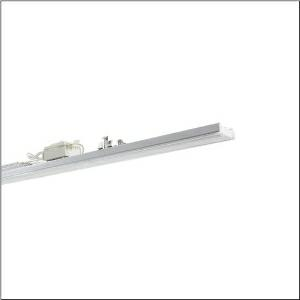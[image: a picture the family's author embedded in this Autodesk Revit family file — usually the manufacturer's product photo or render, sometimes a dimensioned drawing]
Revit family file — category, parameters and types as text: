
# Revit family: licross_r__21_recessed_mo_52te14dn49xg_1976
name_source: partatom
category: Lighting Fixtures
units: mm (PartAtom-declared; Revit-internal decimal feet)

## family parameters
Cut with Voids When Loaded = No
Host = Face
Light Source = No
Part Type = Normal
Room Calculation Point = No
Round Connector Dimension = Use Diameter
Shared = No

## types (1)
- --- (1 x LED, 9470 lm, 58 W, 4000K)
    Apparent Load = 58 VA
    CIE Flux Codes = 56 84 97 100 100
    Color Rendering = 80
    Color Temperature = 4000K
    Default Elevation = 1800 mm
    Description = Licross® 21 Recessed MO, luminaire insert, of sheet steel, galvanised, coil coated, white, length: 1.500mm, width: 66mm, height: 67mm, LED rated luminous flux: 9.470lm, light colour: 840, control gear: DALI 2, with plug, 5-pole, with phase selection, mains connection: 220..240V, AC, 50/60Hz, rated input power: 58W, halogen-free wiring, primary light control with lens, of plastic, primary optical cover: cover, of PMMA, light emission: direct distribution, primary light characteristic: asymmetric, protection rating (complete): IP54, insulation class (complete): insulation class I (protective earthing), certification: CE, ENEC, VDE, UKCA, protection symbol: D if used in an environment with non-conductive dust loads with corresponding accessories, impact resistance: IK06, permissible ambient temperature for indoor applications: -25..+35°C, corresponds to IFS (International Featured Standards) requirements for safety and quality in the food industry, reducing of maximum allowable ambient temperature of 5°C with ceiling mounting, LABS conformity tested according to VDMA 24364:2018-05, packaging unit: 1 piece
    Height = 58 mm
    Lamp = 1 x LED
    Lamp Light Flux = 9470 lm
    Lamp Power = 58 W
    Lamp count = 1
    Length = 1500 mm
    Luminous efficacy = 163 lm/W
    Manufacturer = Siteco
    ModVariant = No
    Model = 52TE14DN49XG
    Mounting Place = Ceiling
    Mounting Type = Pendant
    Number of Poles = 1
    OnlyDefault = Yes
    Power Factor = 1
    Product Name = Licross® 21 Recessed MO
    Product group = luminaire insert
    ProductGroupID = 902
    Protection Class = Protection class I
    Protection Degree = IP 54
    RLX_Detail_Level = 1
    RLX_Emergency_Light_Flux = 0 lm
    RLX_Emergency_Type = 0
    RLX_Emergency_Type_DB = No
    RlxData = <blob elided: 24985 chars, md5=86eb0b27>
    Socket = socket
    Standby Power = 0 W
    System Light Flux = 9470 lm
    System Power = 58 W
    Type Comments = factory setting: luminous flux: 100 % | dim-lin: 254 | 390 mA
    Type Image = l_1296930.jpg
    URL = http://relux.com
    VarID = @adj_127716
    Voltage = 0 V
    Weight = 0.00 kg
    Width = 66 mm

## geometry (parser evidence)
native form markers: Blend x4, Sweep x11
no freeform markers — native parametric forms only
